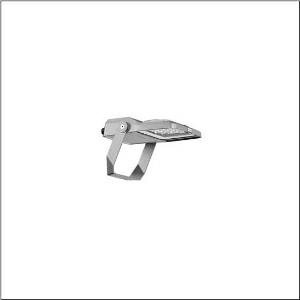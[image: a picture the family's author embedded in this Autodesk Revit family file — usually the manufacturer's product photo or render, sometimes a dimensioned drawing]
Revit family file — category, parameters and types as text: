
# Revit family: floodlight_fl_21_iq_micro___rs12_5xa7762a2b1a_2903
name_source: partatom
category: Lighting Fixtures
units: mm (PartAtom-declared; Revit-internal decimal feet)

## family parameters
Cut with Voids When Loaded = No
Host = Face
Light Source = No
Part Type = Normal
Room Calculation Point = No
Round Connector Dimension = Use Diameter
Shared = No

## types (1)
- --- (1 x LED, 3090 lm, 23.1 W, 3000K)
    Apparent Load = 23 VA
    CIE Flux Codes = 79 92 99 100 100
    Color Rendering = 70
    Color Temperature = 3000K
    Default Elevation = 1800 mm
    Description = Floodlight FL 21 iQ micro, floodlight, primary light control with lens, of PMMA, primary optical cover: protective disc, of toughened safety glass, transparent, light distribution: RS12, light emission: direct distribution, installation type: surface-mounted, lamps: LED, High Power LED, rated values: 3.090lm | 23,1W | 133,8lm/W (begin service life); end service life: 3.090lm | 23,8W; at 50% lumin. flux: 1.545lm | 11W | 140,5lm/W, colour temperature: 3000K, colour rendering: CRI > 70, light colour: 730, light setting 1 begin service life: 100% | 3.090lm | 23,1W | 133,8lm/W | 3.000K, light setting 1 end service life: 23,8W, further light settings possible, control: Auto-Match, Temp-Guard, Night-Set, Smart-Wire, Desk-Remote (wireless, voltage-free reading and setting of iQ features in the workshop via application-optimized NFC function/RFID function), optimised constant luminous flux control (CLO 2.0), Street-Remote, pre-setting: linear dimming characteristic, with terminal, 6-pole, mains connection: 220..240V, AC, 50/60Hz, luminaire housing, of diecast aluminium, powder-coated, SITECO metallic grey (DB 702S), corrosivity category C5 mid according to DIN EN ISO 12944suitable for swimming poolschlorine-resistant, sealing non-destructively replaceable, mounting bracket, of steel, galvanised, powder-coated, SITECO metallic grey (DB 702S), protection rating (complete): IP66, insulation class (complete): insulation class II (safety insulation), certification: CE, ENEC, VDE, protection symbol: D, impact resistance: IK07, permissible operating ambient temperature: -40..+40°C, permissible operating ambient temperature for outdoor applications: -40..+50°C, standard: DIN EN 12944, LABS conformity tested according to VDMA 24364:2018-05, packaging unit: 1 piece

Light Distribution: RS12
    Height = 65 mm
    Lamp = 1 x LED
    Lamp Light Flux = 3090 lm
    Lamp Power = 23.1 W
    Lamp count = 1
    Length = 312 mm
    Luminous efficacy = 134 lm/W
    Manufacturer = Siteco
    ModVariant = No
    Model = 5XA7762A2B1A
    Number of Poles = 1
    OnlyDefault = Yes
    Power Factor = 1
    Product Name = Floodlight FL 21 iQ micro | RS12
    Product group = floodlight | pylon annexe
    ProductGroupID = 6201
    Protection Class = Protection class II
    Protection Degree = IP 66
    RLX_Detail_Level = 1
    RLX_Emergency_Light_Flux = 0 lm
    RLX_Emergency_Type = 0
    RLX_Emergency_Type_DB = No
    RlxData = <blob elided: 75129 chars, md5=4c22d340>
    Socket = socket
    Standby Power = 0 W
    System Light Flux = 3090 lm
    System Power = 23 W
    Type Comments = factory setting: luminous flux: 100 % | dim-lin: 254 | 455 mA
    Type Image = l_1006880.jpg
    URL = http://relux.com
    VarID = @adj_179749
    Voltage = 0 V
    Weight = 0.00 kg
    Width = 230 mm

## geometry (parser evidence)
native form markers: Blend x4, Sweep x11
no freeform markers — native parametric forms only
